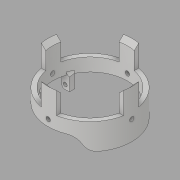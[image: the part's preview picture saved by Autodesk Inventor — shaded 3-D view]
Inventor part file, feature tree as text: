
AUTODESK INVENTOR PART (.ipt)
format: ipt  version: 2017 (Build 210142000, 142)  size: 273,920 bytes
history: native  units: in
note: dims shown in document units (in); Inventor stores cm internally (conversion verified against a paired STEP export)
features: sketch x7, extrude x6, fillet x3, hole x1, chamfer x1
ambient origin geometry x8: Origin, YZ Plane, XZ Plane, XY Plane, X Axis, Y Axis, Z Axis, Center Point
bodies: Solid1 (feature_tree)
feature tree (18):
  extrude  "Extrusion1"  Depth=0.2in
  extrude  "Extrusion2"  Depth=1.5in
  hole  "Hole2"  [1 undecoded]
  fillet  "Fillet1"  Radius=0.6in
  extrude  "Extrusion3"  Depth=0.2in
  fillet  "Fillet2"  Radius=0.125in
  fillet  "Fillet3"  Radius=0.6871in
  extrude  "Extrusion4"  Depth=0.625in
  extrude  "Extrusion5"  Depth=0.2in
  extrude  "Extrusion6"  Depth=0.3in
  chamfer  "Chamfer1"  Distance=1.0in
  sketch  "Sketch1"  dims[d0=3.45in d1=0.2in]
  sketch  "Sketch2"  dims[d2=0.6in d3=0.0in d5=1.5in]
  sketch  "Sketch3"  dims[d6=0.25in d7=1.1in d8=0.6in d9=0.0in]
  sketch  "Sketch4"  dims[d10=0.19in]
  sketch  "Sketch5"  dims[d19=0.18in d20=0.75in d21=0.375in d22=0.25in d23=0.5635in d24=1.0in d25=0.8108in d26=0.2in d27=0.125in d28=0.6871in]
  sketch  "Sketch6"  dims[d29=0.6in d30=0.0in d31=0.625in]
  sketch  "Sketch7"  dims[d32=0.625in d33=0.2in d34=0.3in d35=1.0in d36=0.0in d37=0.2in d38=0.3in d39=1.0in d40=0.0in d41=0.7in d42=1.5748in d44=360.0deg d46=1.0in d47=0.0in d48=0.2in d49=0.125in d50=45.0deg]
note: 1 required parameter value undecoded (feature->parameter linkage not recoverable at this tier; creation-order binding heuristic only, values carry confidence <= 0.55)
